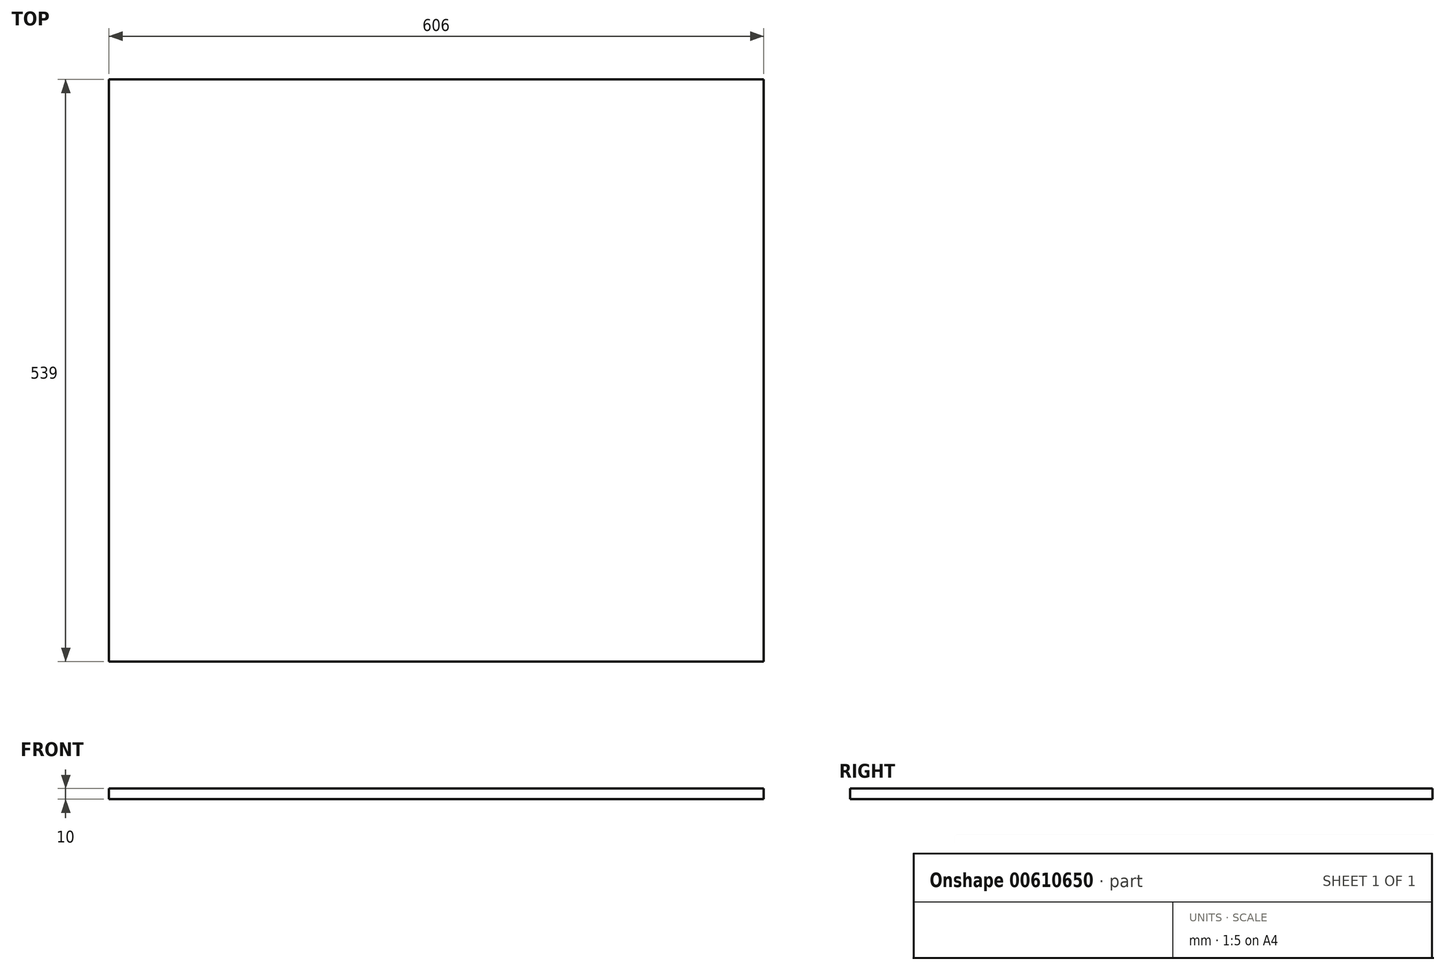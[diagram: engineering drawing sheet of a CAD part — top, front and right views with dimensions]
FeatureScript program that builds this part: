
annotation { "Feature Type Name" : "Feature", "Feature Type Description" : "" }
export const myFeature = defineFeature(function(context is Context, id is Id, definition is map)
    precondition{}
    {
        {
            var Q0;
            Q0=qCreatedBy(makeId("Top.planeOp"),FACE);
            var sketch = newSketch(context, id + "F0", { "sketchPlane" : qUnion([Q0])});
            skLineSegment(sketch, "E0.bottom", {"start": v(-336.36, 210.6) * mm, "end": v(269.64, 210.6) * mm});
            skLineSegment(sketch, "E0.top", {"start": v(-336.36, -328.4) * mm, "end": v(269.64, -328.4) * mm});
            skLineSegment(sketch, "E0.left", {"start": v(-336.36, 210.6) * mm, "end": v(-336.36, -328.4) * mm});
            skLineSegment(sketch, "E0.right", {"start": v(269.64, 210.6) * mm, "end": v(269.64, -328.4) * mm});
            skSolve(sketch);
        }
        {
            var Q0;
            Q0=makeQuery(id+"F0.imprint","IMPRINT",FACE,{"disambiguationData":[TD([[makeQuery(id+"F0.imprint","IMPRINT",EDGE,{"derivedFrom":sQuery(id+"F0.wireOp",EDGE,"E0.bottom")}),-1.0]])]});
            extrude(context, id + "F1", {"entities" : qUnion([Q0]), "depth" : 10 * mm, "offsetDistance" : 25 * mm});
        }
    });
